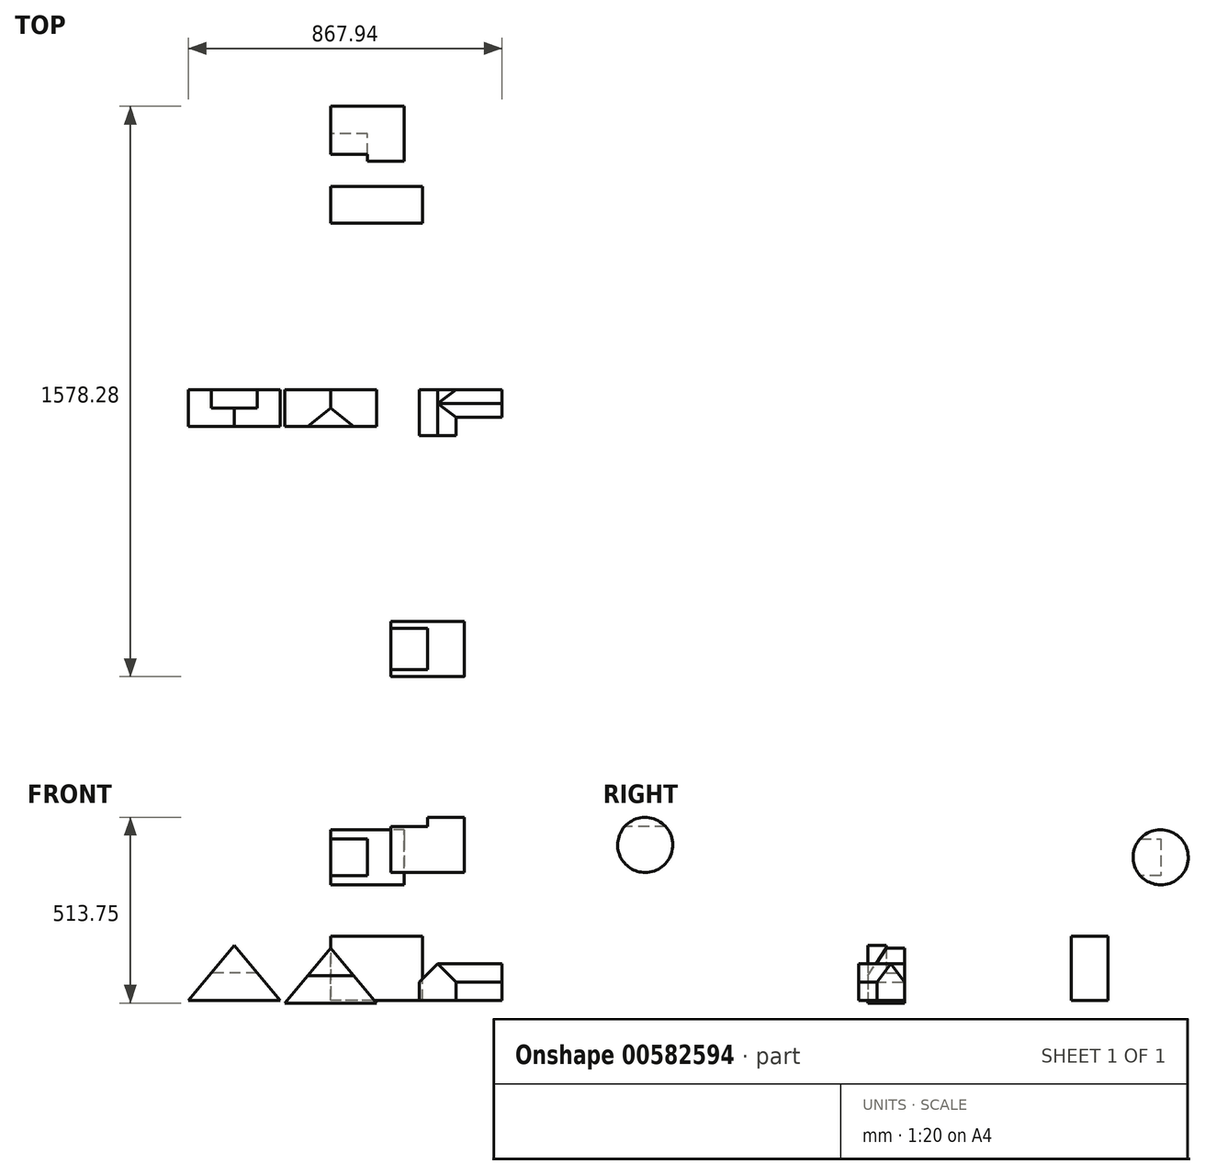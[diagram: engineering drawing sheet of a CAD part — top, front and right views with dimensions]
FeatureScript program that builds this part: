
annotation { "Feature Type Name" : "Feature", "Feature Type Description" : "" }
export const myFeature = defineFeature(function(context is Context, id is Id, definition is map)
    precondition{}
    {
        {
            var Q0;
            Q0=qCreatedBy(makeId("Front.planeOp"),FACE);
            var sketch = newSketch(context, id + "F0", { "sketchPlane" : qUnion([Q0])});
            skLineSegment(sketch, "E0", {"start": v(-560.85, 0) * mm, "end": v(-306.85, 0) * mm});
            skLineSegment(sketch, "E1", {"start": v(-306.85, 0) * mm, "end": v(-306.85, 152.4) * mm});
            skLineSegment(sketch, "E2", {"start": v(-306.85, 152.4) * mm, "end": v(-560.85, 152.4) * mm});
            skLineSegment(sketch, "E3", {"start": v(-560.85, 152.4) * mm, "end": v(-560.85, 0) * mm});
            skLineSegment(sketch, "E4", {"start": v(-433.85, 152.4) * mm, "end": v(-560.85, 0) * mm});
            skLineSegment(sketch, "E5", {"start": v(-433.85, 152.4) * mm, "end": v(-306.85, 0) * mm});
            skSolve(sketch);
        }
        {
            var Q0;
            Q0=makeQuery(id+"F0.imprint","IMPRINT",FACE,{"disambiguationData":[TD([[makeQuery(id+"F0.imprint","IMPRINT",EDGE,{"derivedFrom":sQuery(id+"F0.wireOp",EDGE,"E0")}),1.0]])]});
            extrude(context, id + "F1", {"entities" : qUnion([Q0]), "depth" : 101.6 * mm, "offsetDistance" : 25.4 * mm});
        }
        {
            var Q0;
            Q0=makeQuery(id+"F1.opExtrude","CAP_FACE",FACE,{"disambiguationData":[OSD([sQuery(id+"F0.wireOp",EDGE,"E0"),sQuery(id+"F0.wireOp",EDGE,"E4"),sQuery(id+"F0.wireOp",EDGE,"E5")])],"isStart":true});
            var sketch = newSketch(context, id + "F2", { "sketchPlane" : qUnion([Q0])});
            skLineSegment(sketch, "E6", {"start": v(370.35, 76.2) * mm, "end": v(497.35, 76.2) * mm});
            skSolve(sketch);
        }
        {
            var Q0;
            Q0 = qSketchRegion(id + "F2", true);
            var Q1;
            {var subQ0=sQuery(id+"F2.wireOp",EDGE,"E6");Q1=makeQuery(id+"F2.imprint","IMPRINT",FACE,{"disambiguationData":[TD([[makeQuery(id+"F2.imprint","IMPRINT",EDGE,{"derivedFrom":subQ0}),1.0]])]});}
            extrude(context, id + "F3", {"entities" : qUnion([Q0, Q1]), "operationType" : NewBodyOperationType.REMOVE, "oppositeDirection" : true, "depth" : 50.8 * mm, "offsetDistance" : 25.4 * mm});
        }
        {
            var Q0;
            Q0=qCreatedBy(makeId("Front.planeOp"),FACE);
            var sketch = newSketch(context, id + "F4", { "sketchPlane" : qUnion([Q0])});
            skLineSegment(sketch, "E7", {"start": v(-39.52, -7.31) * mm, "end": v(-293.52, -7.31) * mm});
            skLineSegment(sketch, "E8", {"start": v(-293.52, -7.31) * mm, "end": v(-293.52, 145.09) * mm});
            skLineSegment(sketch, "E9", {"start": v(-293.52, 145.09) * mm, "end": v(-39.52, 145.09) * mm});
            skLineSegment(sketch, "E10", {"start": v(-39.52, 145.09) * mm, "end": v(-39.52, -7.31) * mm});
            skLineSegment(sketch, "E11", {"start": v(-166.52, 145.09) * mm, "end": v(-39.52, -7.31) * mm});
            skLineSegment(sketch, "E12", {"start": v(-166.52, 145.09) * mm, "end": v(-293.52, -7.31) * mm});
            skSolve(sketch);
        }
        {
            var Q0;
            Q0=makeQuery(id+"F4.imprint","IMPRINT",FACE,{"disambiguationData":[TD([[makeQuery(id+"F4.imprint","IMPRINT",EDGE,{"derivedFrom":sQuery(id+"F4.wireOp",EDGE,"E7")}),-1.0]])]});
            extrude(context, id + "F5", {"entities" : qUnion([Q0]), "depth" : 101.6 * mm, "offsetDistance" : 25.4 * mm});
        }
        {
            var Q0;
            Q0=makeQuery(id+"F5.opExtrude","CAP_EDGE",EDGE,{"disambiguationData":[OSD([sQuery(id+"F4.wireOp",EDGE,"E7")])],"isStart":false});
            cPoint(context, id + "F6", {"entities" : qUnion([Q0]), "parameter" : 0.5});
        }
        {
            var Q0;
            Q0=makeQuery(id+"F5.opExtrude","CAP_VERTEX",VERTEX,{"disambiguationData":[OSD([sQuery(id+"F4.wireOp",EDGE,"E9"),sQuery(id+"F4.wireOp",EDGE,"E11"),sQuery(id+"F4.wireOp",EDGE,"E12")])],"isStart":false});
            var Q1;
            Q1=makeQuery(id+"F5.opExtrude","CAP_VERTEX",VERTEX,{"disambiguationData":[OSD([sQuery(id+"F4.wireOp",EDGE,"E9"),sQuery(id+"F4.wireOp",EDGE,"E11"),sQuery(id+"F4.wireOp",EDGE,"E12")])],"isStart":true});
            var Q2;
            Q2 = qCreatedBy(id + "F6" ,VERTEX);
            cPlane(context, id + "F7", {"entities" : qUnion([Q0, Q1, Q2]), "cplaneType" : CPlaneType.THREE_POINT, "offset" : 25.4 * mm, "width" : 152.4 * mm, "height" : 152.4 * mm});
        }
        {
            var Q0;
            Q0=qCreatedBy(id+"F7.planeOp",FACE);
            var sketch = newSketch(context, id + "F8", { "sketchPlane" : qUnion([Q0])});
            skLineSegment(sketch, "E13.0", {"start": v(-101.6, 145.09) * mm, "end": v(-101.6, -7.31) * mm});
            skPoint(sketch, "E14.0", {"position": v(0, 145.09) * mm});
            skLineSegment(sketch, "E15", {"start": v(-101.6, 68.89) * mm, "end": v(-50.8, 145.09) * mm});
            skLineSegment(sketch, "E16", {"start": v(-50.8, 145.09) * mm, "end": v(-101.6, 145.09) * mm});
            skSolve(sketch);
        }
        {
            var Q0;
            Q0 = qSketchRegion(id + "F8", true);
            extrude(context, id + "F9", {"entities" : qUnion([Q0]), "operationType" : NewBodyOperationType.REMOVE, "endBound" : BoundingType.SYMMETRIC, "oppositeDirection" : true, "depth" : 152.4 * mm, "offsetDistance" : 25.4 * mm});
        }
        {
            var Q0;
            Q0=qCreatedBy(makeId("Front.planeOp"),FACE);
            var sketch = newSketch(context, id + "F10", { "sketchPlane" : qUnion([Q0])});
            skLineSegment(sketch, "E17", {"start": v(78.5, 0) * mm, "end": v(180.1, 0) * mm});
            skLineSegment(sketch, "E18", {"start": v(180.1, 0) * mm, "end": v(180.1, 50.8) * mm});
            skLineSegment(sketch, "E19", {"start": v(78.5, 0) * mm, "end": v(78.5, 50.8) * mm});
            skLineSegment(sketch, "E20", {"start": v(78.5, 50.8) * mm, "end": v(129.3, 101.6) * mm});
            skLineSegment(sketch, "E21", {"start": v(180.1, 50.8) * mm, "end": v(129.3, 101.6) * mm});
            skSolve(sketch);
        }
        {
            var Q0;
            Q0=makeQuery(id+"F10.imprint","IMPRINT",FACE,{"disambiguationData":[TD([[makeQuery(id+"F10.imprint","IMPRINT",EDGE,{"derivedFrom":sQuery(id+"F10.wireOp",EDGE,"E17")}),1.0]])]});
            extrude(context, id + "F11", {"entities" : qUnion([Q0]), "depth" : 127 * mm, "offsetDistance" : 25.4 * mm});
        }
        {
            var Q0;
            Q0=makeQuery(id+"F11.opExtrude","SWEPT_FACE",FACE,{"disambiguationData":[OSD([sQuery(id+"F10.wireOp",EDGE,"E18")])]});
            cPlane(context, id + "F12", {"entities" : qUnion([Q0]), "cplaneType" : CPlaneType.OFFSET, "offset" : 127 * mm, "width" : 152.4 * mm, "height" : 152.4 * mm});
        }
        {
            var Q0;
            Q0=qCreatedBy(id+"F12.planeOp",FACE);
            var sketch = newSketch(context, id + "F13", { "sketchPlane" : qUnion([Q0])});
            skLineSegment(sketch, "E22", {"start": v(0, 0) * mm, "end": v(-76.2, 0) * mm});
            skLineSegment(sketch, "E23", {"start": v(-76.2, 0) * mm, "end": v(-76.2, 50.8) * mm});
            skLineSegment(sketch, "E24", {"start": v(0, 0) * mm, "end": v(0, 50.8) * mm});
            skLineSegment(sketch, "E25", {"start": v(-76.2, 50.8) * mm, "end": v(-38.1, 101.6) * mm});
            skLineSegment(sketch, "E26", {"start": v(-38.1, 101.6) * mm, "end": v(0, 50.8) * mm});
            skSolve(sketch);
        }
        {
            var Q0;
            Q0 = qSketchRegion(id + "F13", true);
            extrude(context, id + "F14", {"entities" : qUnion([Q0]), "operationType" : NewBodyOperationType.ADD, "oppositeDirection" : true, "depth" : 177.8 * mm, "offsetDistance" : 25.4 * mm});
        }
        {
            var Q0;
            Q0=qCreatedBy(makeId("Right.planeOp"),FACE);
            var sketch = newSketch(context, id + "F15", { "sketchPlane" : qUnion([Q0])});
            skCircle(sketch, "E27", {"center": v(-718, 430.24) * mm, "radius": 76.2 * mm});
            skLineSegment(sketch, "E28", {"start": v(-718, 481.04) * mm, "end": v(-661.21, 481.04) * mm});
            skLineSegment(sketch, "E29", {"start": v(-661.21, 481.04) * mm, "end": v(-774.8, 481.04) * mm});
            skSolve(sketch);
        }
        {
            var Q0;
            Q0 = qSketchRegion(id + "F15", true);
            extrude(context, id + "F16", {"entities" : qUnion([Q0]), "depth" : 203.2 * mm, "offsetDistance" : 25.4 * mm});
        }
        {
            var Q0;
            {var subQ0=sQuery(id+"F15.wireOp",EDGE,"E29");var subQ4=makeQuery(id+"F15.imprint","IMPRINT",VERTEX,{"derivedFrom":subQ0});Q0=makeQuery(id+"F15.imprint","IMPRINT",FACE,{"disambiguationData":[TD([[makeQuery(id+"F15.imprint","IMPRINT",EDGE,{"disambiguationData":[TD([[subQ4,1.0]])],"derivedFrom":subQ0}),1.0]])]});}
            extrude(context, id + "F17", {"entities" : qUnion([Q0]), "operationType" : NewBodyOperationType.ADD, "depth" : 25.4 * mm, "offsetDistance" : 25.4 * mm});
        }
        {
            var Q0;
            {var subQ0=sQuery(id+"F15.wireOp",EDGE,"E29");var subQ4=makeQuery(id+"F15.imprint","IMPRINT",VERTEX,{"derivedFrom":subQ0});Q0=makeQuery(id+"F15.imprint","IMPRINT",FACE,{"disambiguationData":[TD([[makeQuery(id+"F15.imprint","IMPRINT",EDGE,{"disambiguationData":[TD([[subQ4,1.0]])],"derivedFrom":subQ0}),-1.0]])]});}
            extrude(context, id + "F18", {"entities" : qUnion([Q0]), "operationType" : NewBodyOperationType.REMOVE, "depth" : 101.6 * mm, "offsetDistance" : 25.4 * mm});
        }
        {
            var Q0;
            Q0=qCreatedBy(id+"F7.planeOp",FACE);
            var sketch = newSketch(context, id + "F19", { "sketchPlane" : qUnion([Q0])});
            skCircle(sketch, "E30", {"center": v(707.87, 396.06) * mm, "radius": 76.2 * mm});
            skLineSegment(sketch, "E31", {"start": v(707.87, 396.06) * mm, "end": v(707.87, 472.26) * mm});
            skLineSegment(sketch, "E32", {"start": v(707.87, 396.06) * mm, "end": v(707.87, 319.86) * mm});
            skLineSegment(sketch, "E33", {"start": v(651.08, 446.86) * mm, "end": v(707.87, 446.86) * mm});
            skLineSegment(sketch, "E34", {"start": v(707.87, 345.26) * mm, "end": v(651.08, 345.26) * mm});
            skSolve(sketch);
        }
        {
            var Q0;
            {var subQ3=sQuery(id+"F19.wireOp",EDGE,"E33");Q0=makeQuery(id+"F19.imprint","IMPRINT",FACE,{"disambiguationData":[TD([[makeQuery(id+"F19.imprint","IMPRINT",EDGE,{"derivedFrom":subQ3}),1.0]])]});}
            var Q1;
            {var subQ3=sQuery(id+"F19.wireOp",EDGE,"E34");Q1=makeQuery(id+"F19.imprint","IMPRINT",FACE,{"disambiguationData":[TD([[makeQuery(id+"F19.imprint","IMPRINT",EDGE,{"derivedFrom":subQ3}),1.0]])]});}
            var Q2;
            {var subQ1=sQuery(id+"F19.wireOp",EDGE,"E31");var subQ4=sQuery(id+"F19.wireOp",EDGE,"E30");var subQ5=makeQuery(id+"F19.imprint","INTERSECT",VERTEX,{"derivedFrom":[subQ4,subQ1]});Q2=makeQuery(id+"F19.imprint","IMPRINT",FACE,{"disambiguationData":[TD([[makeQuery(id+"F19.imprint","IMPRINT",EDGE,{"disambiguationData":[TD([[subQ5,1.0]])],"derivedFrom":subQ4}),1.0]])]});}
            var Q3;
            {var subQ0=sQuery(id+"F19.wireOp",EDGE,"E33");Q3=makeQuery(id+"F19.imprint","IMPRINT",FACE,{"disambiguationData":[TD([[makeQuery(id+"F19.imprint","IMPRINT",EDGE,{"derivedFrom":subQ0}),-1.0]])]});}
            extrude(context, id + "F20", {"entities" : qUnion([Q0, Q1, Q2, Q3]), "depth" : 203.2 * mm, "offsetDistance" : 25.4 * mm});
        }
        {
            var Q0;
            {var subQ0=sQuery(id+"F19.wireOp",EDGE,"E33");Q0=makeQuery(id+"F19.imprint","IMPRINT",FACE,{"disambiguationData":[TD([[makeQuery(id+"F19.imprint","IMPRINT",EDGE,{"derivedFrom":subQ0}),-1.0]])]});}
            extrude(context, id + "F21", {"entities" : qUnion([Q0]), "operationType" : NewBodyOperationType.REMOVE, "depth" : 101.6 * mm, "offsetDistance" : 25.4 * mm});
        }
        {
            var Q0;
            Q0=qCreatedBy(id+"F7.planeOp",FACE);
            var sketch = newSketch(context, id + "F22", { "sketchPlane" : qUnion([Q0])});
            skLineSegment(sketch, "E35", {"start": v(460.16, 177.8) * mm, "end": v(561.76, 177.8) * mm});
            skLineSegment(sketch, "E36", {"start": v(561.76, 177.8) * mm, "end": v(561.76, 0) * mm});
            skLineSegment(sketch, "E37", {"start": v(561.76, 0) * mm, "end": v(460.16, 0) * mm});
            skLineSegment(sketch, "E38", {"start": v(460.16, 0) * mm, "end": v(460.16, 177.8) * mm});
            skSolve(sketch);
        }
        {
            var Q0;
            Q0=makeQuery(id+"F22.imprint","IMPRINT",FACE,{"disambiguationData":[TD([[makeQuery(id+"F22.imprint","IMPRINT",EDGE,{"derivedFrom":sQuery(id+"F22.wireOp",EDGE,"E35")}),-1.0]])]});
            extrude(context, id + "F23", {"entities" : qUnion([Q0]), "depth" : 254 * mm, "offsetDistance" : 25.4 * mm});
        }
    });
